# Revit family: Table-Teknion-CWRF_Reception_Full_Enclosure-R2016
name_source: partatom
category: Furniture
revit_build: Autodesk Revit 2018 (Build: 20190510_1515(x64)
units: mm (PartAtom-declared; Revit-internal decimal feet)

## family parameters
Always vertical = Yes
Cut with Voids When Loaded = No
OmniClass Number = 23.40.20.00
OmniClass Title = General Furniture and Specialties
Room Calculation Point = No
Shared = Yes
Work Plane-Based = No

## types (3) — shared parameters
Assembly Code = E2020200
Manufacturer = Teknion
Manufacturer Fax = 416.661.4586
Part Number = CWRF
Product Documentation Link = https://assets.teknion.com
Product Line = Reception
Product Page URL = https://www.teknion.com
Series = Custom Wood
Sustainability Data = https://www.teknion.com
URL = www.teknion.com
Unit Weight URL = http://www.teknion.com
Warranty = http://www.teknion.com

## per-type parameters (varying)
| type | Center | Description | Left | Left & Center | Model | Not Center | Right | Right & Center |
| Left Transaction Counter | No | Teknion Reception with Full Enclosure, Left Transaction Counter | Yes | Yes | CWRF_____L | Yes | No | No |
| Right Transaction Counter | No | Teknion Reception with Full Enclosure, Right Transaction Counter | No | No | CWRF_____R | Yes | Yes | Yes |
| Center Transaction Counter | Yes | Teknion Reception with Full Enclosure, Center Transaction Counter | No | Yes | CWRF_____C | No | No | Yes |

## geometry (parser evidence)
native form markers: Blend x33, Sweep x5
no freeform markers — native parametric forms only
